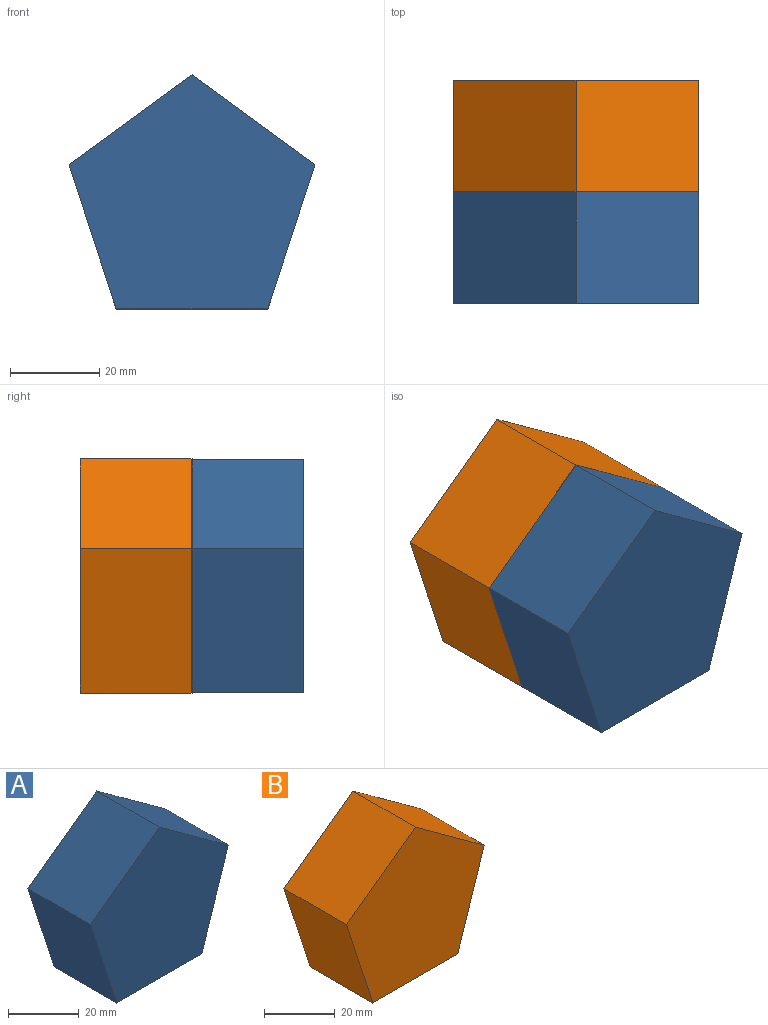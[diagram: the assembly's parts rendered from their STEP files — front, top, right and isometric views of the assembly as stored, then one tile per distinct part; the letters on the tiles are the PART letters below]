
ASSEMBLY  parts=2 mates=1
PART A: 7 faces, bbox 55x25x52.3 mm
  f0: plane 34x25mm, normal (0,0,-1), area 850mm2, adj f1,f4,f5,f6
  f1: plane 32.34x25mm, normal (0.95,0,-0.31), area 850mm2, adj f0,f2,f5,f6
  f2: plane 27.51x25mm, normal (0.59,0,0.81), area 850mm2, adj f1,f3,f5,f6
  f3: plane 27.51x25mm, normal (-0.59,0,0.81), area 850mm2, adj f2,f4,f5,f6
  f4: plane 32.34x25mm, normal (-0.95,0,-0.31), area 850mm2, adj f0,f3,f5,f6
  f5: plane 55.01x52.32mm, normal (0,-1,0), area 1988.9mm2, adj f0,f1,f2,f3,f4
  f6: plane 55.01x52.32mm, normal (0,1,0), area 1988.9mm2, adj f0,f1,f2,f3,f4
PART B: 7 faces, bbox 55x25x52.3 mm
  f0: plane 27.5x25mm, normal (0.59,0,0.81), area 850.1mm2, adj f1,f4,f5,f6
  f1: plane 27.5x25mm, normal (-0.59,0,0.81), area 850.1mm2, adj f0,f2,f5,f6
  f2: plane 32.35x25mm, normal (-0.95,0,-0.31), area 850.4mm2, adj f1,f3,f5,f6
  f3: plane 33.96x25mm, normal (0,0,-1), area 849mm2, adj f2,f4,f5,f6
  f4: plane 32.35x25mm, normal (0.95,0,-0.31), area 850.4mm2, adj f0,f3,f5,f6
  f5: plane 55x52.35mm, normal (0,-1,0), area 1988.9mm2, adj f0,f1,f2,f3,f4
  f6: plane 55x52.35mm, normal (0,1,0), area 1988.9mm2, adj f0,f1,f2,f3,f4
PLACE A t=(39.48,-26.78,14.06)mm
PLACE B t=(-36.82,-1.78,14.08)mm
MATE fastened A.f6 <-> B.f5  axis (0,1,0) through (-4.82,-26.78,13.04)mm
